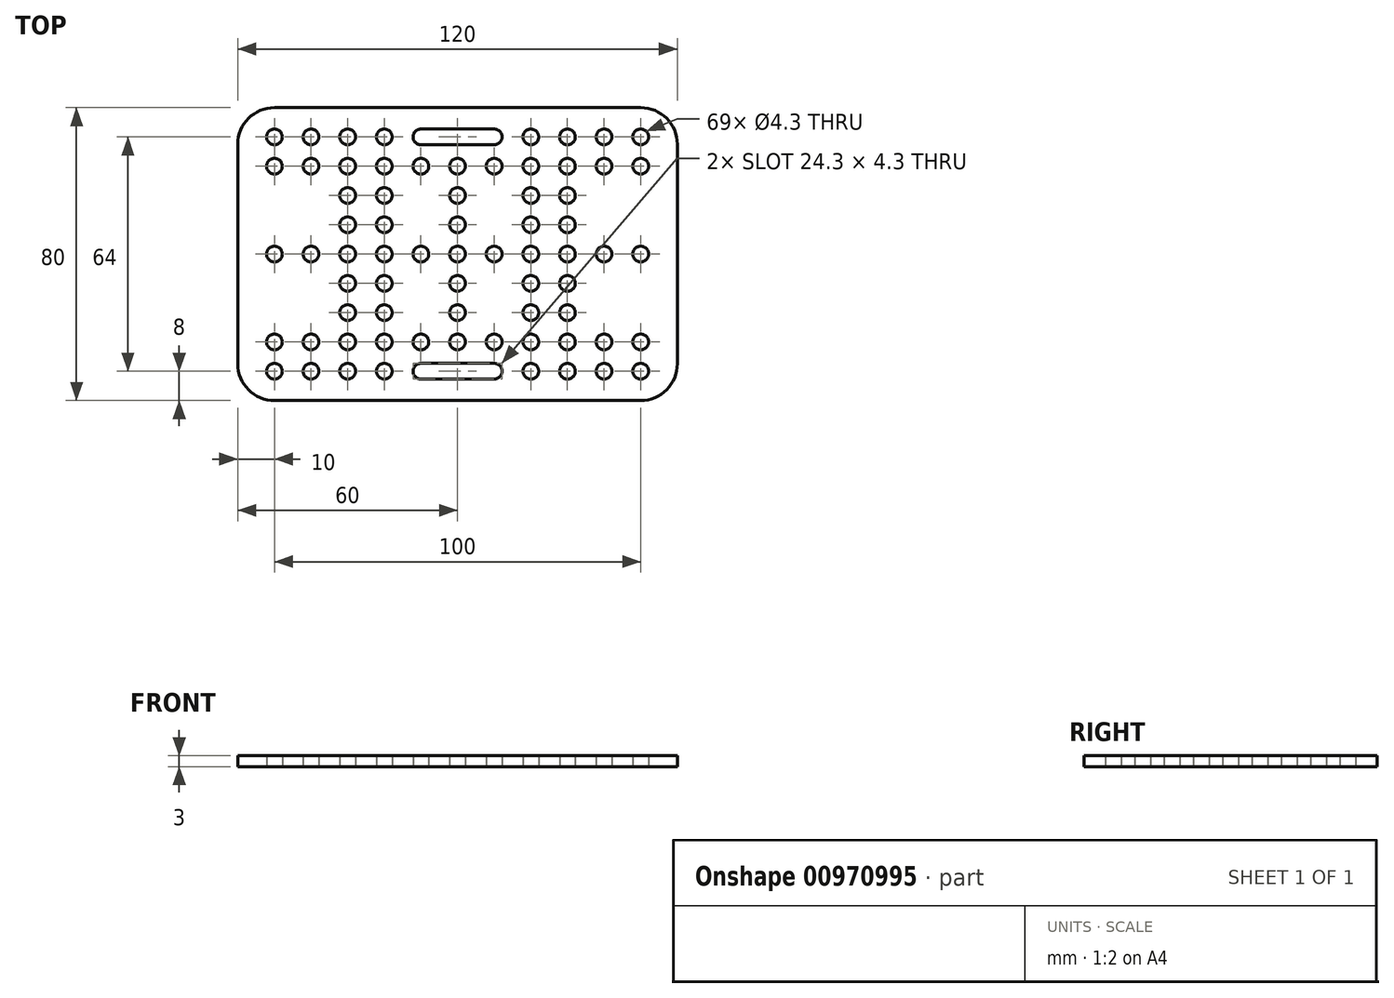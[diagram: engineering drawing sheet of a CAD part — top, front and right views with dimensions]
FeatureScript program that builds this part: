
annotation { "Feature Type Name" : "Feature", "Feature Type Description" : "" }
export const myFeature = defineFeature(function(context is Context, id is Id, definition is map)
    precondition{}
    {
        {
            var Q0;
            Q0=qCreatedBy(makeId("Top.planeOp"),FACE);
            var sketch = newSketch(context, id + "F0", { "sketchPlane" : qUnion([Q0])});
            skLineSegment(sketch, "E0.bottom", {"start": v(50, -40) * mm, "end": v(-50, -40) * mm});
            skLineSegment(sketch, "E0.top", {"start": v(50, 40) * mm, "end": v(-50, 40) * mm});
            skLineSegment(sketch, "E0.left", {"start": v(60, -30) * mm, "end": v(60, 30) * mm});
            skLineSegment(sketch, "E0.right", {"start": v(-60, -30) * mm, "end": v(-60, 30) * mm});
            skPoint(sketch, "E0.middle", {"position": v(0, 0) * mm});
            skCircle(sketch, "E1", {"center": v(0, 0) * mm, "radius": 2.15 * mm});
            skCircle(sketch, "E2", {"center": v(0, 8) * mm, "radius": 2.15 * mm});
            skCircle(sketch, "E3", {"center": v(0, 16) * mm, "radius": 2.15 * mm});
            skCircle(sketch, "E4", {"center": v(0, 24) * mm, "radius": 2.15 * mm});
            skCircle(sketch, "E5", {"center": v(0, 32) * mm, "radius": 2.15 * mm});
            skCircle(sketch, "E6", {"center": v(-10, 0) * mm, "radius": 2.15 * mm});
            skCircle(sketch, "E7", {"center": v(-20, 0) * mm, "radius": 2.15 * mm});
            skCircle(sketch, "E8", {"center": v(-30, 0) * mm, "radius": 2.15 * mm});
            skCircle(sketch, "E9", {"center": v(-40, 0) * mm, "radius": 2.15 * mm});
            skCircle(sketch, "E10", {"center": v(-50, 0) * mm, "radius": 2.15 * mm});
            skCircle(sketch, "E11", {"center": v(-30, 8) * mm, "radius": 2.15 * mm});
            skCircle(sketch, "E12", {"center": v(-30, 16) * mm, "radius": 2.15 * mm});
            skCircle(sketch, "E13", {"center": v(-30, 32) * mm, "radius": 2.15 * mm});
            skCircle(sketch, "E14", {"center": v(-30, 24) * mm, "radius": 2.15 * mm});
            skCircle(sketch, "E15", {"center": v(-20, 8) * mm, "radius": 2.15 * mm});
            skCircle(sketch, "E16", {"center": v(-20, 16) * mm, "radius": 2.15 * mm});
            skCircle(sketch, "E17", {"center": v(-20, 24) * mm, "radius": 2.15 * mm});
            skCircle(sketch, "E18", {"center": v(-20, 32) * mm, "radius": 2.15 * mm});
            skCircle(sketch, "E19", {"center": v(-10, 24) * mm, "radius": 2.15 * mm});
            skCircle(sketch, "E20", {"center": v(-10, 32) * mm, "radius": 2.15 * mm});
            skCircle(sketch, "E21", {"center": v(-40, 24) * mm, "radius": 2.15 * mm});
            skCircle(sketch, "E22", {"center": v(-50, 24) * mm, "radius": 2.15 * mm});
            skCircle(sketch, "E23", {"center": v(-40, 32) * mm, "radius": 2.15 * mm});
            skCircle(sketch, "E24", {"center": v(-50, 32) * mm, "radius": 2.15 * mm});
            skLineSegment(sketch, "E25", {"start": v(-10, 34.15) * mm, "end": v(0, 34.15) * mm});
            skLineSegment(sketch, "E26", {"start": v(0, 34.15) * mm, "end": v(0, 29.85) * mm});
            skLineSegment(sketch, "E27", {"start": v(0, 29.85) * mm, "end": v(-10, 29.85) * mm});
            skCircle(sketch, "E28.MirrorC", {"center": v(30, 0) * mm, "radius": 2.15 * mm});
            skCircle(sketch, "E29.MirrorC", {"center": v(20, 0) * mm, "radius": 2.15 * mm});
            skCircle(sketch, "E30.MirrorC", {"center": v(40, 0) * mm, "radius": 2.15 * mm});
            skCircle(sketch, "E31.MirrorC", {"center": v(10, 0) * mm, "radius": 2.15 * mm});
            skCircle(sketch, "E32.MirrorC", {"center": v(20, 8) * mm, "radius": 2.15 * mm});
            skCircle(sketch, "E33.MirrorC", {"center": v(50, 0) * mm, "radius": 2.15 * mm});
            skCircle(sketch, "E34.MirrorC", {"center": v(10, 24) * mm, "radius": 2.15 * mm});
            skCircle(sketch, "E35.MirrorC", {"center": v(30, 24) * mm, "radius": 2.15 * mm});
            skCircle(sketch, "E36.MirrorC", {"center": v(20, 24) * mm, "radius": 2.15 * mm});
            skCircle(sketch, "E37.MirrorC", {"center": v(20, 16) * mm, "radius": 2.15 * mm});
            skCircle(sketch, "E38.MirrorC", {"center": v(30, 16) * mm, "radius": 2.15 * mm});
            skCircle(sketch, "E39.MirrorC", {"center": v(30, 32) * mm, "radius": 2.15 * mm});
            skCircle(sketch, "E40.MirrorC", {"center": v(20, 32) * mm, "radius": 2.15 * mm});
            skCircle(sketch, "E41.MirrorC", {"center": v(30, 8) * mm, "radius": 2.15 * mm});
            skCircle(sketch, "E42.MirrorC", {"center": v(10, 32) * mm, "radius": 2.15 * mm});
            skCircle(sketch, "E43.MirrorC", {"center": v(50, 32) * mm, "radius": 2.15 * mm});
            skCircle(sketch, "E44.MirrorC", {"center": v(50, 24) * mm, "radius": 2.15 * mm});
            skCircle(sketch, "E45.MirrorC", {"center": v(40, 24) * mm, "radius": 2.15 * mm});
            skCircle(sketch, "E46.MirrorC", {"center": v(40, 32) * mm, "radius": 2.15 * mm});
            skLineSegment(sketch, "E47", {"start": v(0, 29.85) * mm, "end": v(10, 29.85) * mm});
            skLineSegment(sketch, "E48", {"start": v(0, 34.15) * mm, "end": v(10, 34.15) * mm});
            skLineSegment(sketch, "E49.MirrorCS", {"start": v(0, -34.15) * mm, "end": v(0, -29.85) * mm});
            skCircle(sketch, "E50.MirrorC", {"center": v(0, -24) * mm, "radius": 2.15 * mm});
            skCircle(sketch, "E51.MirrorC", {"center": v(0, -16) * mm, "radius": 2.15 * mm});
            skCircle(sketch, "E52.MirrorC", {"center": v(20, -8) * mm, "radius": 2.15 * mm});
            skCircle(sketch, "E53.MirrorC", {"center": v(20, -16) * mm, "radius": 2.15 * mm});
            skCircle(sketch, "E54.MirrorC", {"center": v(-10, -32) * mm, "radius": 2.15 * mm});
            skCircle(sketch, "E55.MirrorC", {"center": v(10, -24) * mm, "radius": 2.15 * mm});
            skCircle(sketch, "E56.MirrorC", {"center": v(30, -8) * mm, "radius": 2.15 * mm});
            skCircle(sketch, "E57.MirrorC", {"center": v(-20, -24) * mm, "radius": 2.15 * mm});
            skCircle(sketch, "E58.MirrorC", {"center": v(-40, -32) * mm, "radius": 2.15 * mm});
            skLineSegment(sketch, "E59.MirrorCS", {"start": v(0, -29.85) * mm, "end": v(10, -29.85) * mm});
            skCircle(sketch, "E60.MirrorC", {"center": v(20, -24) * mm, "radius": 2.15 * mm});
            skCircle(sketch, "E61.MirrorC", {"center": v(30, -16) * mm, "radius": 2.15 * mm});
            skLineSegment(sketch, "E62.MirrorCS", {"start": v(0, -34.15) * mm, "end": v(10, -34.15) * mm});
            skCircle(sketch, "E63.MirrorC", {"center": v(-20, -16) * mm, "radius": 2.15 * mm});
            skCircle(sketch, "E64.MirrorC", {"center": v(-50, -24) * mm, "radius": 2.15 * mm});
            skCircle(sketch, "E65.MirrorC", {"center": v(-20, -32) * mm, "radius": 2.15 * mm});
            skCircle(sketch, "E66.MirrorC", {"center": v(-10, -24) * mm, "radius": 2.15 * mm});
            skCircle(sketch, "E67.MirrorC", {"center": v(40, -32) * mm, "radius": 2.15 * mm});
            skCircle(sketch, "E68.MirrorC", {"center": v(50, -24) * mm, "radius": 2.15 * mm});
            skLineSegment(sketch, "E69.MirrorCS", {"start": v(-10, -34.15) * mm, "end": v(0, -34.15) * mm});
            skCircle(sketch, "E70.MirrorC", {"center": v(20, -32) * mm, "radius": 2.15 * mm});
            skCircle(sketch, "E71.MirrorC", {"center": v(50, -32) * mm, "radius": 2.15 * mm});
            skCircle(sketch, "E72.MirrorC", {"center": v(-30, -16) * mm, "radius": 2.15 * mm});
            skCircle(sketch, "E73.MirrorC", {"center": v(-40, -24) * mm, "radius": 2.15 * mm});
            skCircle(sketch, "E74.MirrorC", {"center": v(-50, -32) * mm, "radius": 2.15 * mm});
            skCircle(sketch, "E75.MirrorC", {"center": v(-30, -32) * mm, "radius": 2.15 * mm});
            skCircle(sketch, "E76.MirrorC", {"center": v(10, -32) * mm, "radius": 2.15 * mm});
            skLineSegment(sketch, "E77.MirrorCS", {"start": v(0, -29.85) * mm, "end": v(-10, -29.85) * mm});
            skCircle(sketch, "E78.MirrorC", {"center": v(30, -24) * mm, "radius": 2.15 * mm});
            skCircle(sketch, "E79.MirrorC", {"center": v(0, -8) * mm, "radius": 2.15 * mm});
            skCircle(sketch, "E80.MirrorC", {"center": v(30, -32) * mm, "radius": 2.15 * mm});
            skCircle(sketch, "E81.MirrorC", {"center": v(40, -24) * mm, "radius": 2.15 * mm});
            skCircle(sketch, "E82.MirrorC", {"center": v(-20, -8) * mm, "radius": 2.15 * mm});
            skCircle(sketch, "E83.MirrorC", {"center": v(-30, -8) * mm, "radius": 2.15 * mm});
            skCircle(sketch, "E84.MirrorC", {"center": v(-30, -24) * mm, "radius": 2.15 * mm});
            skCircle(sketch, "E85.MirrorC", {"center": v(0, -32) * mm, "radius": 2.15 * mm});
            skPoint(sketch, "E86.visualSharp", {"position": v(-60, 40) * mm});
            skArc(sketch, "E86.filletArc", {"start": v(-50, 40) * mm, "mid": v(-57.07, 37.07) * mm, "end": v(-60, 30) * mm});
            skPoint(sketch, "E87.visualSharp", {"position": v(60, 40) * mm});
            skArc(sketch, "E87.filletArc", {"start": v(60, 30) * mm, "mid": v(57.07, 37.07) * mm, "end": v(50, 40) * mm});
            skPoint(sketch, "E88.visualSharp", {"position": v(60, -40) * mm});
            skArc(sketch, "E88.filletArc", {"start": v(50, -40) * mm, "mid": v(57.07, -37.07) * mm, "end": v(60, -30) * mm});
            skPoint(sketch, "E89.visualSharp", {"position": v(-60, -40) * mm});
            skArc(sketch, "E89.filletArc", {"start": v(-60, -30) * mm, "mid": v(-57.07, -37.07) * mm, "end": v(-50, -40) * mm});
            skSolve(sketch);
        }
        {
            var Q0;
            Q0 = qSketchRegion(id + "F0", true);
            extrude(context, id + "F1", {"entities" : qUnion([Q0]), "depth" : 3 * mm, "offsetDistance" : 25 * mm});
        }
    });
